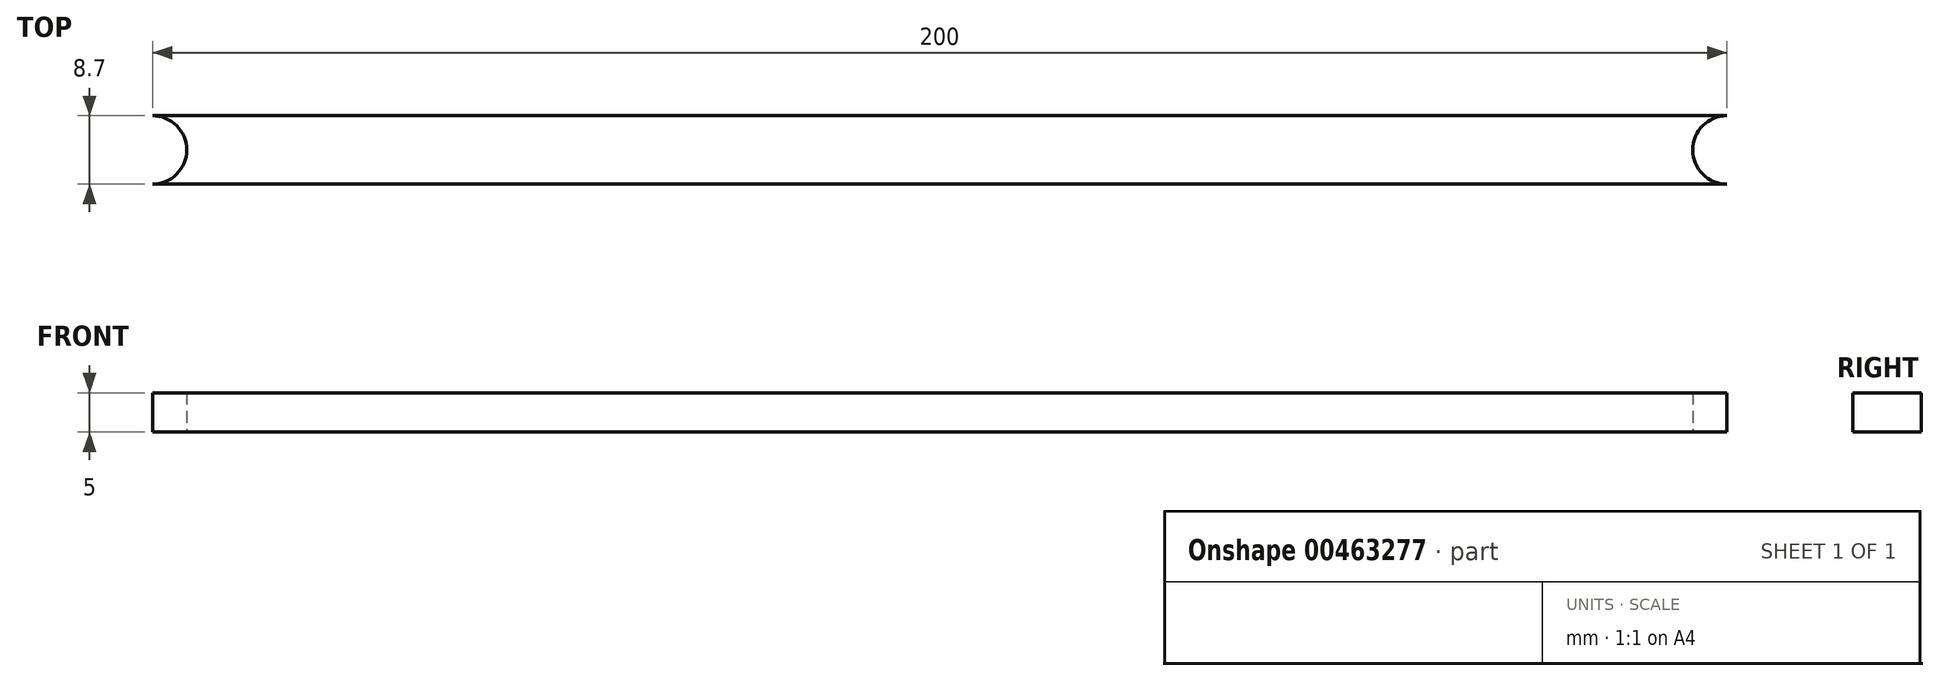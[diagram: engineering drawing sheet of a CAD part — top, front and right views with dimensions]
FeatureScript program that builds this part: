
annotation { "Feature Type Name" : "Feature", "Feature Type Description" : "" }
export const myFeature = defineFeature(function(context is Context, id is Id, definition is map)
    precondition{}
    {
        {
            var Q0;
            Q0=qCreatedBy(makeId("Top.planeOp"),FACE);
            var sketch = newSketch(context, id + "F0", { "sketchPlane" : qUnion([Q0])});
            skArc(sketch, "E0", {"start": v(-100, -4.35) * mm, "mid": v(-95.65, 0) * mm, "end": v(-100, 4.35) * mm});
            skLineSegment(sketch, "E1", {"start": v(-100, 4.35) * mm, "end": v(0, 4.35) * mm});
            skLineSegment(sketch, "E2.MirrorCS", {"start": v(-100, -4.35) * mm, "end": v(0, -4.35) * mm});
            skArc(sketch, "E3.MirrorCS", {"start": v(100, -4.35) * mm, "mid": v(95.65, 0) * mm, "end": v(100, 4.35) * mm});
            skLineSegment(sketch, "E4.MirrorCS", {"start": v(100, -4.35) * mm, "end": v(0, -4.35) * mm});
            skLineSegment(sketch, "E5.MirrorCS", {"start": v(100, 4.35) * mm, "end": v(0, 4.35) * mm});
            skSolve(sketch);
        }
        {
            var Q0;
            Q0 = qSketchRegion(id + "F0", true);
            extrude(context, id + "F1", {"entities" : qUnion([Q0]), "depth" : 5 * mm});
        }
    });
